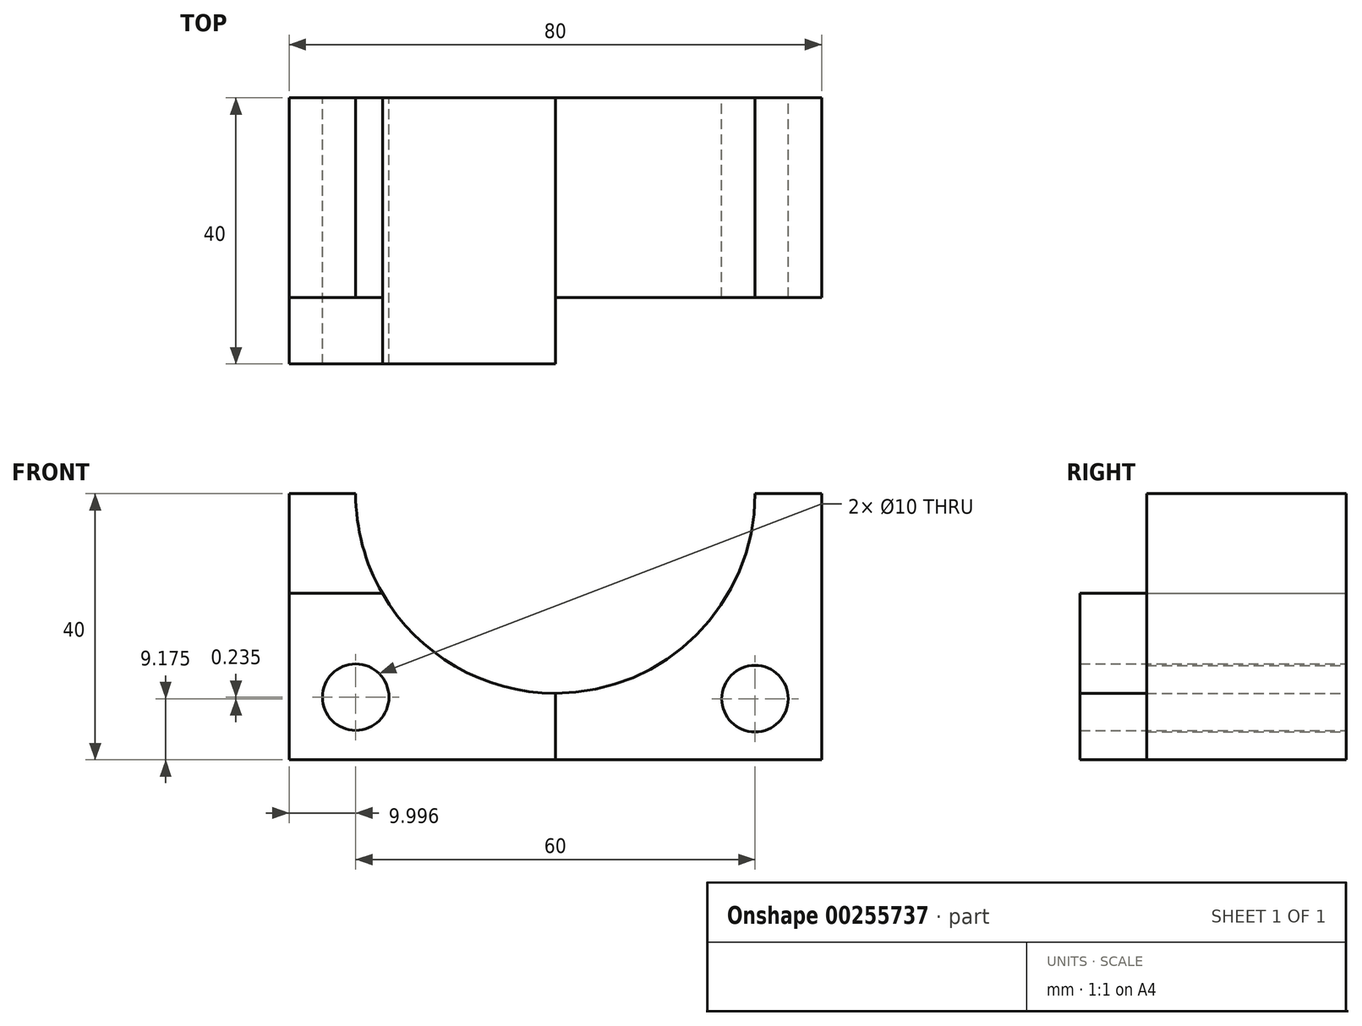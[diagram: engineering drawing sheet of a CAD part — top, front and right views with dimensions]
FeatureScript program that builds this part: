
annotation { "Feature Type Name" : "Feature", "Feature Type Description" : "" }
export const myFeature = defineFeature(function(context is Context, id is Id, definition is map)
    precondition{}
    {
        {
            var Q0;
            Q0=qCreatedBy(makeId("Front.planeOp"),FACE);
            var sketch = newSketch(context, id + "F0", { "sketchPlane" : qUnion([Q0])});
            skLineSegment(sketch, "E0.bottom", {"start": v(-71.18, -31.56) * mm, "end": v(-61.18, -31.56) * mm});
            skLineSegment(sketch, "E0.top", {"start": v(-71.18, -71.56) * mm, "end": v(8.82, -71.56) * mm});
            skLineSegment(sketch, "E0.left", {"start": v(-71.18, -31.56) * mm, "end": v(-71.18, -71.56) * mm});
            skLineSegment(sketch, "E0.right", {"start": v(8.82, -31.56) * mm, "end": v(8.82, -71.56) * mm});
            skArc(sketch, "E1", {"start": v(-61.18, -31.56) * mm, "mid": v(-31.18, -61.56) * mm, "end": v(-1.18, -31.56) * mm});
            skLineSegment(sketch, "E2.trimOffspring", {"start": v(-1.18, -31.56) * mm, "end": v(8.82, -31.56) * mm});
            skCircle(sketch, "E3", {"center": v(-61.18, -62.15) * mm, "radius": 5 * mm});
            skCircle(sketch, "E4", {"center": v(-1.18, -62.38) * mm, "radius": 5 * mm});
            skLineSegment(sketch, "E5", {"start": v(-31.18, -61.56) * mm, "end": v(-31.18, -71.56) * mm});
            skLineSegment(sketch, "E6", {"start": v(-71.18, -46.56) * mm, "end": v(-57.16, -46.56) * mm});
            skSolve(sketch);
        }
        {
            var Q0;
            {var subQ0=sQuery(id+"F0.wireOp",EDGE,"E0.bottom");Q0=makeQuery(id+"F0.imprint","IMPRINT",FACE,{"disambiguationData":[TD([[makeQuery(id+"F0.imprint","IMPRINT",EDGE,{"derivedFrom":subQ0}),-1.0]])]});}
            var Q1;
            {var subQ1=sQuery(id+"F0.wireOp",EDGE,"E0.right");Q1=makeQuery(id+"F0.imprint","IMPRINT",FACE,{"disambiguationData":[TD([[makeQuery(id+"F0.imprint","IMPRINT",EDGE,{"derivedFrom":subQ1}),-1.0]])]});}
            extrude(context, id + "F1", {"entities" : qUnion([Q0, Q1]), "depth" : 30 * mm});
        }
        {
            var Q0;
            Q0=makeQuery(id+"F0.imprint","IMPRINT",FACE,{"disambiguationData":[TD([[makeQuery(id+"F0.imprint","IMPRINT",EDGE,{"derivedFrom":sQuery(id+"F0.wireOp",EDGE,"E3")}),-1.0]])]});
            extrude(context, id + "F2", {"entities" : qUnion([Q0]), "depth" : 40 * mm});
        }
    });
